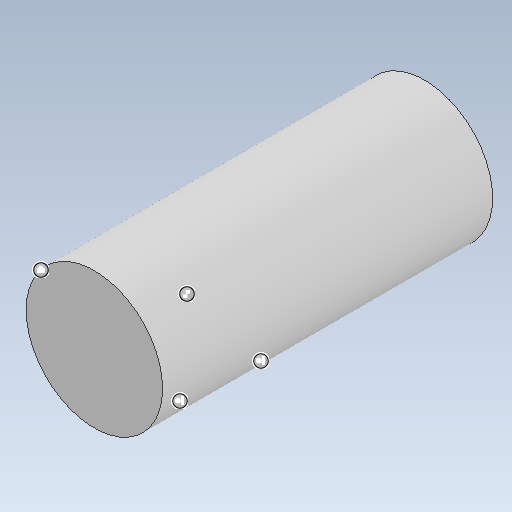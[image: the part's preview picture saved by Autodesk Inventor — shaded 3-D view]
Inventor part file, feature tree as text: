
AUTODESK INVENTOR PART (.ipt)
format: ipt  version: 2021 (Build 250183000, 183)  size: 101,376 bytes
history: native  units: mm
features: extrude x1, sketch x1
ambient origin geometry x8: Origin, YZ Plane, XZ Plane, XY Plane, X Axis, Y Axis, Z Axis, Center Point
bodies: Solid1 (feature_tree)
feature tree (2):
  extrude  "Extrusion1"  TaperAngle=0.0deg  [1 undecoded]
  sketch  "Sketch1"  dims[d2=0.0mm d3=0.0mm d4=0.0mm d9=0.0mm d10=0.0mm]
note: 1 required parameter value undecoded (feature->parameter linkage not recoverable at this tier; creation-order binding heuristic only, values carry confidence <= 0.55)
